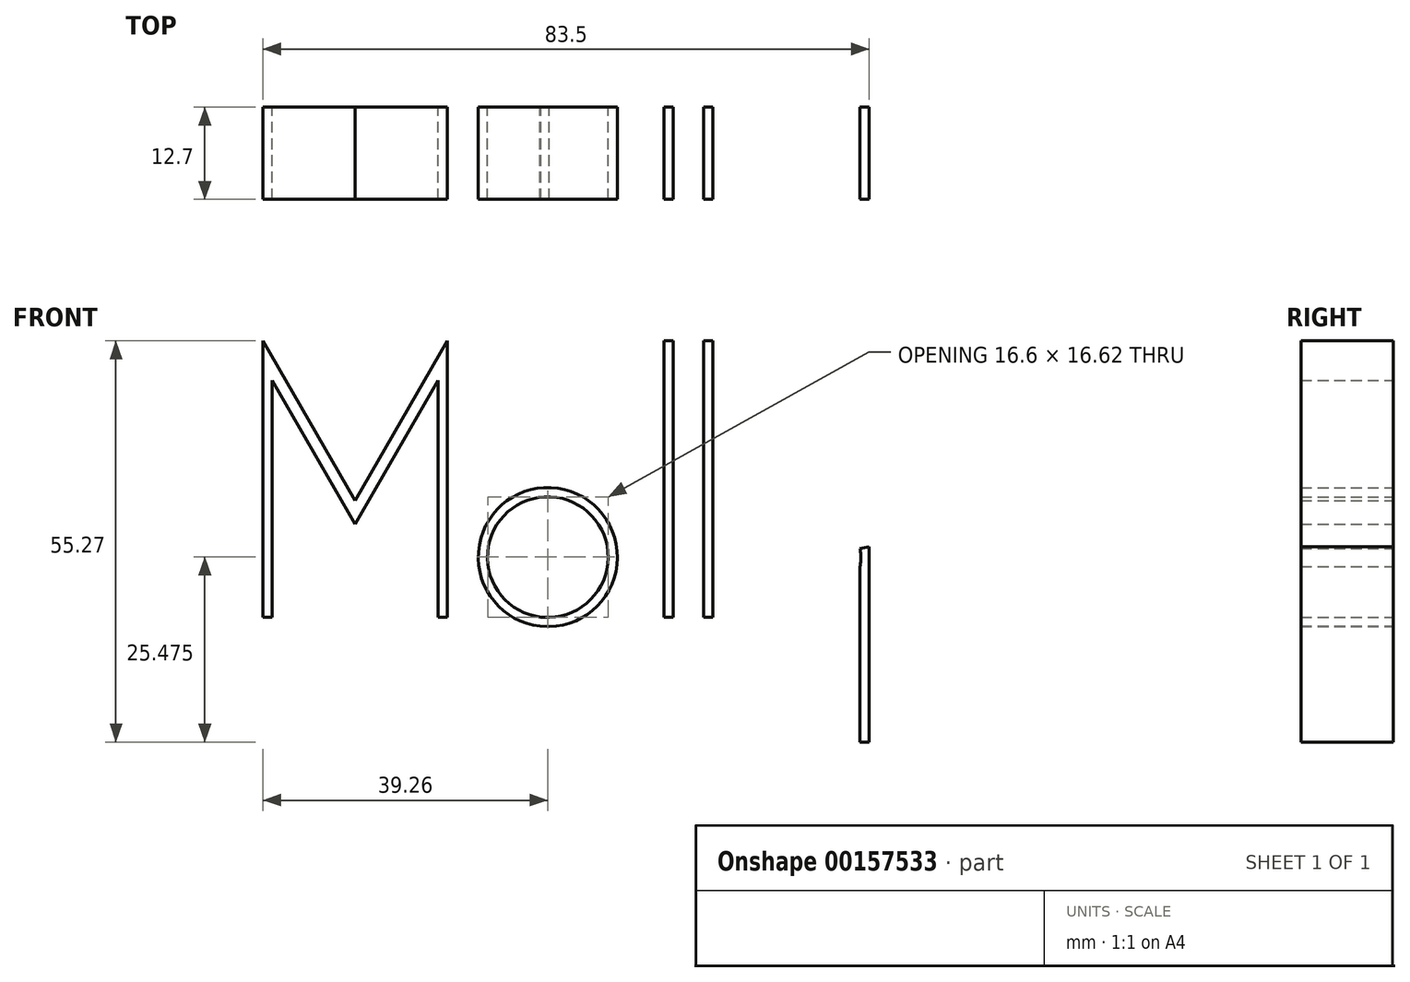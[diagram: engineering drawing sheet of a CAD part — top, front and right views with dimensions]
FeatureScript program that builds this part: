
annotation { "Feature Type Name" : "Feature", "Feature Type Description" : "" }
export const myFeature = defineFeature(function(context is Context, id is Id, definition is map)
    precondition{}
    {
        {
            var Q0;
            Q0=qCreatedBy(makeId("Front.planeOp"),FACE);
            var sketch = newSketch(context, id + "F0", { "sketchPlane" : qUnion([Q0])});
            skLineSegment(sketch, "E0", {"start": v(-60.69, 22) * mm, "end": v(-60.69, -16.1) * mm});
            skLineSegment(sketch, "E1", {"start": v(-47.99, 0) * mm, "end": v(-60.69, 22) * mm});
            skLineSegment(sketch, "E2", {"start": v(-47.99, 0) * mm, "end": v(-35.29, 22) * mm});
            skLineSegment(sketch, "E3", {"start": v(-35.29, 22) * mm, "end": v(-35.29, -16.1) * mm});
            skPoint(sketch, "E4.first.point", {"position": v(-24.42, -16.1) * mm});
            skPoint(sketch, "E4.second.point", {"position": v(-19.88, 0) * mm});
            skPoint(sketch, "E4.third.point", {"position": v(-12.43, -11.77) * mm});
            skLineSegment(sketch, "E5", {"start": v(-4.18, 22) * mm, "end": v(-4.18, -16.1) * mm});
            skLineSegment(sketch, "E6", {"start": v(1.27, 22) * mm, "end": v(1.27, -16.1) * mm});
            skArc(sketch, "E7", {"start": v(15.62, -16.1) * mm, "mid": v(8.6, -13.54) * mm, "end": v(6.48, -6.38) * mm});
            skArc(sketch, "E8", {"start": v(15.62, -16.1) * mm, "mid": v(21.31, -12.8) * mm, "end": v(22.8, -6.38) * mm});
            skLineSegment(sketch, "E9", {"start": v(22.8, -6.38) * mm, "end": v(22.8, -33.27) * mm});
            skLineSegment(sketch, "E10", {"start": v(-4.18, 22) * mm, "end": v(-5.45, 22) * mm});
            skLineSegment(sketch, "E11", {"start": v(-5.45, 22) * mm, "end": v(-5.45, -16.1) * mm});
            skLineSegment(sketch, "E12", {"start": v(-5.45, -16.1) * mm, "end": v(-4.18, -16.1) * mm});
            skLineSegment(sketch, "E13", {"start": v(1.27, 22) * mm, "end": v(0, 22) * mm});
            skLineSegment(sketch, "E14", {"start": v(0, 22) * mm, "end": v(0, -16.1) * mm});
            skLineSegment(sketch, "E15", {"start": v(0, -16.1) * mm, "end": v(1.27, -16.1) * mm});
            skArc(sketch, "E16.0", {"start": v(13.85, -14.85) * mm, "mid": v(9, -12.06) * mm, "end": v(7.73, -6.6) * mm});
            skArc(sketch, "E17.0", {"start": v(13.85, -14.85) * mm, "mid": v(19.78, -12.66) * mm, "end": v(21.56, -6.6) * mm});
            skLineSegment(sketch, "E18", {"start": v(6.48, -6.38) * mm, "end": v(7.73, -6.6) * mm});
            skLineSegment(sketch, "E19", {"start": v(21.56, -6.6) * mm, "end": v(22.8, -6.38) * mm});
            skLineSegment(sketch, "E20", {"start": v(21.56, -6.6) * mm, "end": v(21.56, -33.27) * mm});
            skLineSegment(sketch, "E21", {"start": v(21.56, -33.27) * mm, "end": v(22.8, -33.27) * mm});
            skArc(sketch, "E22", {"start": v(21.56, -33.27) * mm, "mid": v(19.73, -37.94) * mm, "end": v(15.22, -40.15) * mm});
            skArc(sketch, "E23", {"start": v(15.22, -40.15) * mm, "mid": v(9.97, -38.35) * mm, "end": v(7.74, -33.27) * mm});
            skArc(sketch, "E24.0", {"start": v(22.83, -33.27) * mm, "mid": v(20.67, -38.8) * mm, "end": v(15.33, -41.42) * mm});
            skArc(sketch, "E25.0", {"start": v(15.33, -41.42) * mm, "mid": v(9.1, -39.28) * mm, "end": v(6.47, -33.27) * mm});
            skLineSegment(sketch, "E26", {"start": v(6.47, -33.27) * mm, "end": v(7.74, -33.27) * mm});
            skLineSegment(sketch, "E27", {"start": v(-59.42, -16.1) * mm, "end": v(-59.42, 16.56) * mm});
            skLineSegment(sketch, "E28", {"start": v(-59.42, 16.56) * mm, "end": v(-47.99, -3.24) * mm});
            skLineSegment(sketch, "E29", {"start": v(-47.99, -3.24) * mm, "end": v(-36.56, 16.56) * mm});
            skLineSegment(sketch, "E30", {"start": v(-36.56, 16.56) * mm, "end": v(-36.56, -16.1) * mm});
            skLineSegment(sketch, "E31", {"start": v(-36.56, -16.1) * mm, "end": v(-35.29, -16.1) * mm});
            skLineSegment(sketch, "E32", {"start": v(-60.69, -16.1) * mm, "end": v(-59.42, -16.1) * mm});
            skArc(sketch, "E33", {"start": v(-21.26, -16.1) * mm, "mid": v(-13.13, -7.93) * mm, "end": v(-20.99, 0.5) * mm});
            skArc(sketch, "E34.0", {"start": v(-21.23, -17.37) * mm, "mid": v(-11.86, -7.95) * mm, "end": v(-20.92, 1.78) * mm});
            skArc(sketch, "E35", {"start": v(-20.99, 0.5) * mm, "mid": v(-29.73, -7.1) * mm, "end": v(-22.38, -16.05) * mm});
            skArc(sketch, "E36.0", {"start": v(-20.92, 1.78) * mm, "mid": v(-31, -7) * mm, "end": v(-22.52, -17.31) * mm});
            skLineSegment(sketch, "E37", {"start": v(-22.52, -17.31) * mm, "end": v(-21.23, -17.37) * mm});
            skLineSegment(sketch, "E38", {"start": v(-22.38, -16.05) * mm, "end": v(-21.26, -16.1) * mm});
            skLineSegment(sketch, "E39", {"start": v(15.22, -40.15) * mm, "end": v(15.33, -41.42) * mm});
            skLineSegment(sketch, "E40", {"start": v(22.83, -33.27) * mm, "end": v(21.56, -33.27) * mm});
            skSolve(sketch);
        }
        {
            var Q0;
            Q0=makeQuery(id+"F0.imprint","IMPRINT",FACE,{"disambiguationData":[TD([[makeQuery(id+"F0.imprint","IMPRINT",EDGE,{"derivedFrom":sQuery(id+"F0.wireOp",EDGE,"E33")}),-1.0]])]});
            var Q1;
            Q1=makeQuery(id+"F0.imprint","IMPRINT",FACE,{"disambiguationData":[TD([[makeQuery(id+"F0.imprint","IMPRINT",EDGE,{"derivedFrom":sQuery(id+"F0.wireOp",EDGE,"E0")}),1.0]])]});
            var Q2;
            Q2=makeQuery(id+"F0.imprint","IMPRINT",FACE,{"disambiguationData":[TD([[makeQuery(id+"F0.imprint","IMPRINT",EDGE,{"derivedFrom":sQuery(id+"F0.wireOp",EDGE,"E5")}),-1.0]])]});
            var Q3;
            Q3=makeQuery(id+"F0.imprint","IMPRINT",FACE,{"disambiguationData":[TD([[makeQuery(id+"F0.imprint","IMPRINT",EDGE,{"derivedFrom":sQuery(id+"F0.wireOp",EDGE,"E6")}),-1.0]])]});
            var Q4;
            {var subQ2=sQuery(id+"F0.wireOp",EDGE,"E7");Q4=makeQuery(id+"F0.imprint","IMPRINT",FACE,{"disambiguationData":[TD([[makeQuery(id+"F0.imprint","IMPRINT",EDGE,{"derivedFrom":subQ2}),-1.0]])]});}
            var Q5;
            {var subQ0=sQuery(id+"F0.wireOp",EDGE,"E19");Q5=makeQuery(id+"F0.imprint","IMPRINT",FACE,{"disambiguationData":[TD([[makeQuery(id+"F0.imprint","IMPRINT",EDGE,{"derivedFrom":subQ0}),-1.0]])]});}
            var Q6;
            {var subQ5=sQuery(id+"F0.wireOp",EDGE,"E21");Q6=makeQuery(id+"F0.imprint","IMPRINT",FACE,{"disambiguationData":[TD([[makeQuery(id+"F0.imprint","IMPRINT",EDGE,{"derivedFrom":subQ5}),1.0]])]});}
            var Q7;
            {var subQ0=sQuery(id+"F0.wireOp",EDGE,"E20");var subQ1=sQuery(id+"F0.wireOp",EDGE,"E8");var subQ2=makeQuery(id+"F0.imprint","INTERSECT",VERTEX,{"derivedFrom":[subQ1,subQ0]});Q7=makeQuery(id+"F0.imprint","IMPRINT",FACE,{"disambiguationData":[TD([[makeQuery(id+"F0.imprint","IMPRINT",EDGE,{"disambiguationData":[TD([[subQ2,-1.0]])],"derivedFrom":subQ1}),-1.0]])]});}
            var Q8;
            {var subQ3=sQuery(id+"F0.wireOp",EDGE,"E22");Q8=makeQuery(id+"F0.imprint","IMPRINT",FACE,{"disambiguationData":[TD([[makeQuery(id+"F0.imprint","IMPRINT",EDGE,{"derivedFrom":subQ3}),1.0]])]});}
            var Q9;
            Q9=makeQuery(id+"F0.imprint","IMPRINT",FACE,{"disambiguationData":[TD([[makeQuery(id+"F0.imprint","IMPRINT",EDGE,{"derivedFrom":sQuery(id+"F0.wireOp",EDGE,"E23")}),1.0]])]});
            extrude(context, id + "F1", {"entities" : qUnion([Q0, Q1, Q2, Q3, Q4, Q5, Q6, Q7, Q8, Q9]), "endBound" : BoundingType.SYMMETRIC, "depth" : 12.7 * mm});
        }
    });
